# Revit family: Pocket-Panel_Operable-Partition_Moderco_Single
name_source: partatom
category: Doors
units: mm (PartAtom-declared; Revit-internal decimal feet)

## family parameters
Always vertical = No
Classification Number = 23.25.40.17
Cut with Voids When Loaded = No
Room Calculation Point = No
Shared = No
Work Plane-Based = Yes

## types (3) — shared parameters
Assembly Code = C1010300
Construction Details = http://www.arcat.com
Default Elevation = 0' - 0"
Keynote = 10 22 26
Manufacturer = Moderco, Inc
Manufacturer Fax = 450-641-4965 or 800-231-4965
Manufacturer Website = http://moderco.com
Panel Thickness = 0' - 4"
Product Data = http://www.arcat.com
Revision = R1_2015-09
Sales Information = http://moderco.com
Specification = http://www.arcat.com
URL = http://moderco.com
Width = 0' - 0"
zero-valued in all types: Expected Lifespan (Years), Maintenance Schedule (Months), Warranty Duration (Years)

## per-type parameters (varying)
| type | Construction Type | Description | Include Trim | Jamb_Left | Jamb_Right | Swing Away from Pocket | Swing Into Pocket |
| PN-1 | Trimed Edges | Moderco PN-1 Pocket Door as Specified | Yes | 0' - 1 3/4" | 0' - 2 3/8" | Yes | No |
| PA-1 | Trimed Edges | Moderco PA-1 Pocket Door as Specified | Yes | 0' - 2 1/8" | 0' - 2 3/8" | No | Yes |
| P-1 | Trimless Edges | Moderco P-1 Pocket Door as Specified | No | 0' - 4" | 0' - 2 1/2" | No | Yes |

note: column(s) folded — value = type name in every type: Model

## geometry (parser evidence)
native form markers: Sweep x2
no freeform markers — native parametric forms only
